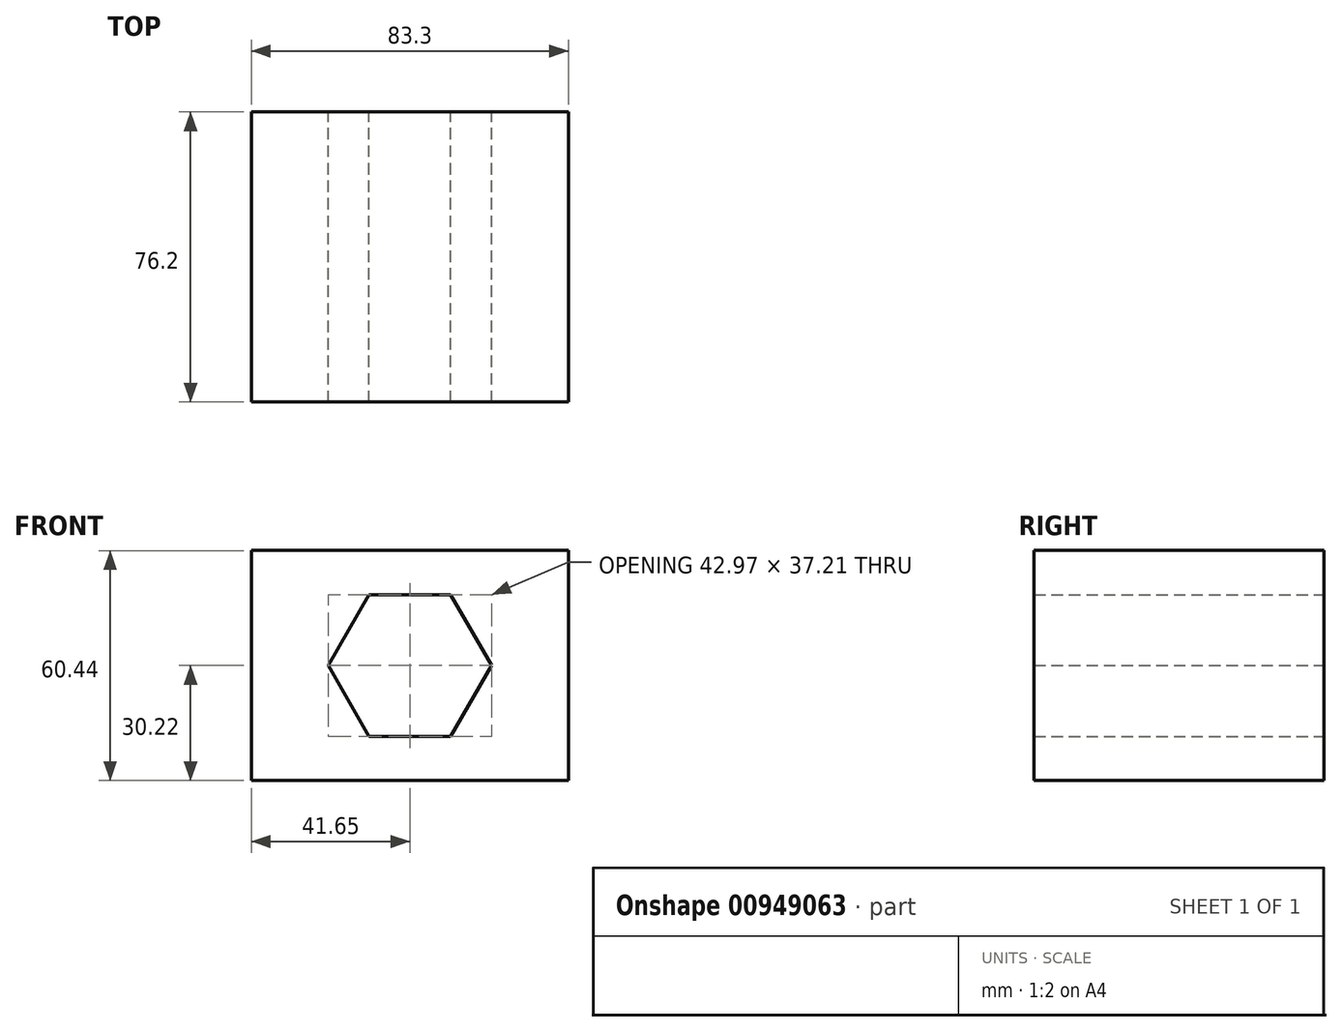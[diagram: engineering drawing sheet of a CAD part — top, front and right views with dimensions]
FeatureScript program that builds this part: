
annotation { "Feature Type Name" : "Feature", "Feature Type Description" : "" }
export const myFeature = defineFeature(function(context is Context, id is Id, definition is map)
    precondition{}
    {
        {
            var Q0;
            Q0=qCreatedBy(makeId("Front.planeOp"),FACE);
            var sketch = newSketch(context, id + "F0", { "sketchPlane" : qUnion([Q0])});
            skLineSegment(sketch, "E0.bottom", {"start": v(-41.65, -30.22) * mm, "end": v(41.65, -30.22) * mm});
            skLineSegment(sketch, "E0.top", {"start": v(-41.65, 30.22) * mm, "end": v(41.65, 30.22) * mm});
            skLineSegment(sketch, "E0.left", {"start": v(-41.65, -30.22) * mm, "end": v(-41.65, 30.22) * mm});
            skLineSegment(sketch, "E0.right", {"start": v(41.65, -30.22) * mm, "end": v(41.65, 30.22) * mm});
            skPoint(sketch, "E0.middle", {"position": v(0, 0) * mm});
            skCircle(sketch, "E1.cCircle", {"center": v(0, 0) * mm, "radius": 21.49 * mm, "construction": true});
            skLineSegment(sketch, "E1.0", {"start": v(21.49, 0) * mm, "end": v(10.74, -18.6) * mm});
            skLineSegment(sketch, "E1.1", {"start": v(10.74, -18.6) * mm, "end": v(-10.74, -18.6) * mm});
            skLineSegment(sketch, "E1.2", {"start": v(-10.74, -18.6) * mm, "end": v(-21.49, 0) * mm});
            skLineSegment(sketch, "E1.3", {"start": v(-21.49, 0) * mm, "end": v(-10.74, 18.6) * mm});
            skLineSegment(sketch, "E1.4", {"start": v(-10.74, 18.6) * mm, "end": v(10.74, 18.6) * mm});
            skLineSegment(sketch, "E1.5", {"start": v(10.74, 18.6) * mm, "end": v(21.49, 0) * mm});
            skSolve(sketch);
        }
        {
            var Q0;
            Q0=makeQuery(id+"F0.imprint","IMPRINT",FACE,{"disambiguationData":[TD([[makeQuery(id+"F0.imprint","IMPRINT",EDGE,{"derivedFrom":sQuery(id+"F0.wireOp",EDGE,"E0.bottom")}),1.0]])]});
            extrude(context, id + "F1", {"entities" : qUnion([Q0]), "depth" : 76.2 * mm, "offsetDistance" : 25.4 * mm});
        }
    });
